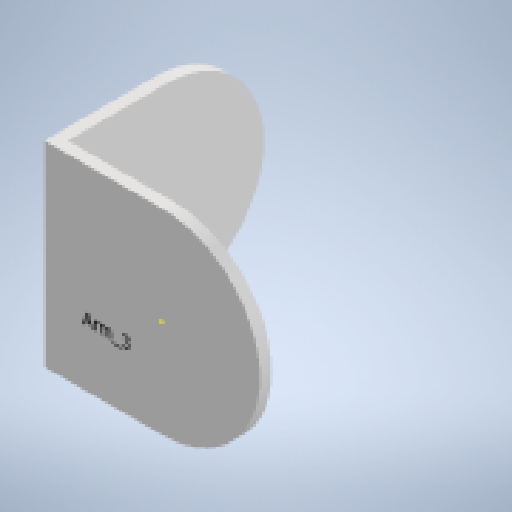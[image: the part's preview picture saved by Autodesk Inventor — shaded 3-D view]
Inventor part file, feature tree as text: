
AUTODESK INVENTOR PART (.ipt)
format: ipt  version: 2023 (Build 270158000, 158)  size: 155,648 bytes
history: native  units: mm
features: sketch x4, extrude x3, other x1, plane x1, projected_geometry x1
ambient origin geometry x8: Origin, YZ Plane, XZ Plane, XY Plane, X Axis, Y Axis, Z Axis, Center Point
bodies: Body1 (feature_tree)
feature tree (10):
  other  "實體1"
  extrude  "擠出1"  Depth=50.0mm
  sketch  "草圖4"
  extrude  "擠出4"  Depth=150.0mm
  plane  "工作平面1"
  extrude  "擠出5"  Depth=5.0mm
  sketch  "草圖1"
  sketch  "草圖5"
  sketch  "草圖6"
  projected_geometry  "投影迴路2"
